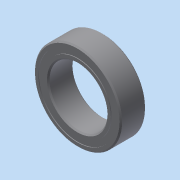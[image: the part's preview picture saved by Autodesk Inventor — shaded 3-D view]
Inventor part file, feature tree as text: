
AUTODESK INVENTOR PART (.ipt)
format: ipt  version: 2015 (Build 190159000, 159)  size: 602,112 bytes
history: native  units: in
note: dims shown in document units (in); Inventor stores cm internally (conversion verified against a paired STEP export)
features: imported_body x16, other x12, revolve x5
ambient origin geometry x8: Origin, YZ Plane, XZ Plane, XY Plane, X Axis, Y Axis, Z Axis, Center Point
bodies: Body1 (feature_tree), Body2 (feature_tree), Body3 (feature_tree), Body4 (feature_tree), Body5 (feature_tree), Body6 (feature_tree), Body7 (feature_tree), Body8 (feature_tree), Body9 (feature_tree), Body10 (feature_tree), Body11 (feature_tree), Body12 (feature_tree), Body13 (feature_tree), Body14 (feature_tree), Body15 (feature_tree), Body16 (feature_tree)
feature tree (33):
  revolve  "Revolve1"  [1 undecoded]
  other  "7804K1151"
  revolve  "Revolve3"  [1 undecoded]
  revolve  "Revolve4"  [1 undecoded]
  other  "CirPattern1[1]"
  other  "CirPattern1[2]"
  other  "CirPattern1[3]"
  other  "CirPattern1[4]"
  other  "CirPattern1[5]"
  other  "CirPattern1[6]"
  other  "CirPattern1[7]"
  other  "CirPattern1[8]"
  other  "CirPattern1[9]"
  other  "CirPattern1[10]"
  other  "CirPattern1[11]"
  revolve  "Revolve5[1]"  [1 undecoded]
  revolve  "Revolve5[2]"  [1 undecoded]
  imported_body  "Base1"
  imported_body  "Base2"
  imported_body  "Base3"
  imported_body  "Base4"
  imported_body  "Base5"
  imported_body  "Base6"
  imported_body  "Base7"
  imported_body  "Base8"
  imported_body  "Base9"
  imported_body  "Base10"
  imported_body  "Base11"
  imported_body  "Base12"
  imported_body  "Base13"
  imported_body  "Base14"
  imported_body  "Base15"
  imported_body  "Base16"
note: 5 required parameter values undecoded (feature->parameter linkage not recoverable at this tier; creation-order binding heuristic only, values carry confidence <= 0.55)
